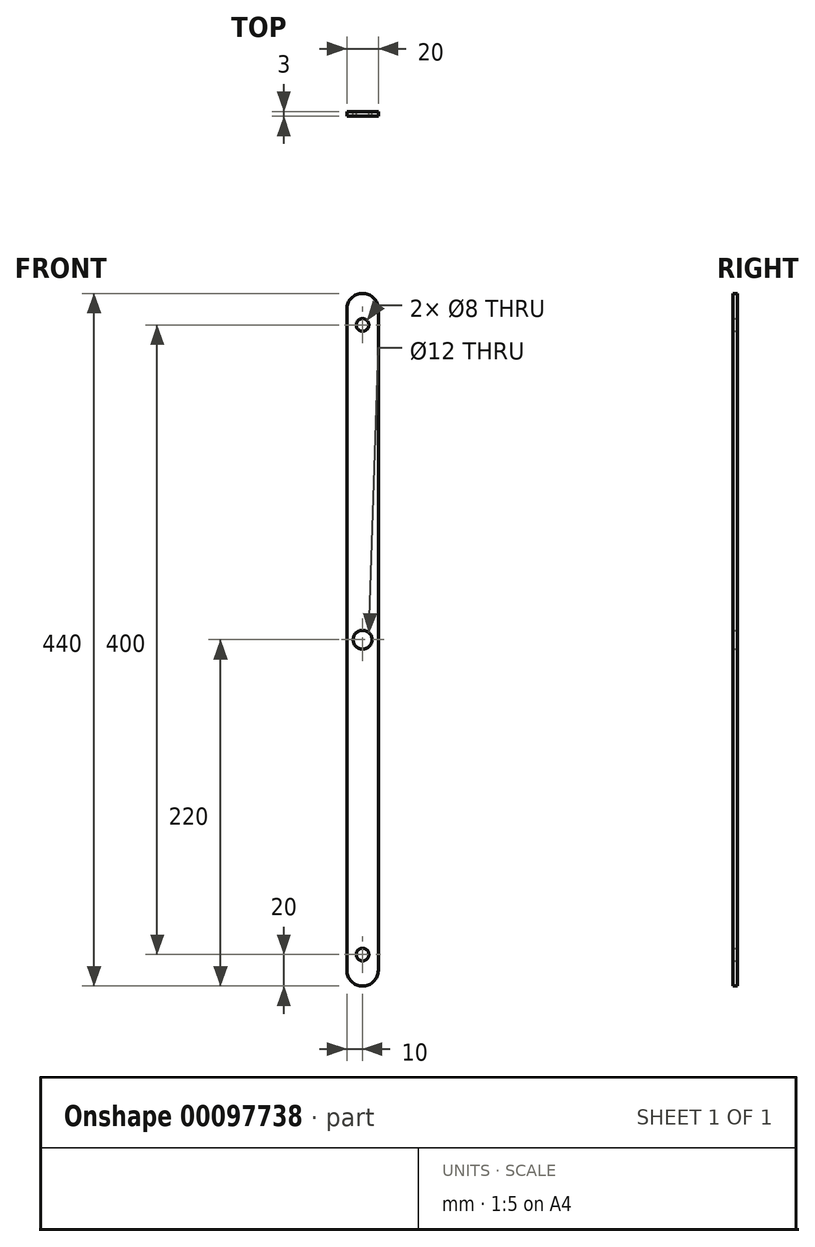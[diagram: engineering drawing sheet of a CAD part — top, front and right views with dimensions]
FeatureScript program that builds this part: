
annotation { "Feature Type Name" : "Feature", "Feature Type Description" : "" }
export const myFeature = defineFeature(function(context is Context, id is Id, definition is map)
    precondition{}
    {
        {
            var Q0;
            Q0=qCreatedBy(makeId("Front.planeOp"),FACE);
            var sketch = newSketch(context, id + "F0", { "sketchPlane" : qUnion([Q0])});
            skLineSegment(sketch, "E0", {"start": v(-10, 210) * mm, "end": v(-10, -210) * mm});
            skArc(sketch, "E1", {"start": v(-10, -210) * mm, "mid": v(0, -220) * mm, "end": v(10, -210) * mm});
            skArc(sketch, "E2", {"start": v(10, 210) * mm, "mid": v(0, 220) * mm, "end": v(-10, 210) * mm});
            skLineSegment(sketch, "E3", {"start": v(10, 210) * mm, "end": v(10, -210) * mm});
            skLineSegment(sketch, "E4", {"start": v(0, 210) * mm, "end": v(0, -210) * mm, "construction": true});
            skCircle(sketch, "E5", {"center": v(0, 0) * mm, "radius": 6 * mm});
            skCircle(sketch, "E6", {"center": v(0, 200) * mm, "radius": 4 * mm});
            skCircle(sketch, "E7", {"center": v(0, -200) * mm, "radius": 4 * mm});
            skSolve(sketch);
        }
        {
            var Q0;
            Q0=makeQuery(id+"F0.imprint","IMPRINT",FACE,{"disambiguationData":[TD([[makeQuery(id+"F0.imprint","IMPRINT",EDGE,{"derivedFrom":sQuery(id+"F0.wireOp",EDGE,"E0")}),1.0]])]});
            extrude(context, id + "F1", {"entities" : qUnion([Q0]), "endBound" : BoundingType.SYMMETRIC, "depth" : 3 * mm});
        }
    });
